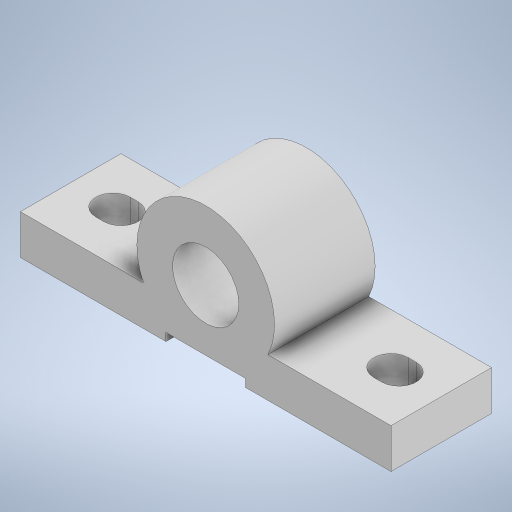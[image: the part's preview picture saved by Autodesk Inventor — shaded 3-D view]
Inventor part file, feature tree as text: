
AUTODESK INVENTOR PART (.ipt)
format: ipt  version: 2023 (Build 270158000, 158)  size: 265,728 bytes
history: native  units: mm
features: extrude x2, sketch x2, other x1
ambient origin geometry x8: Origin, YZ Plane, XZ Plane, XY Plane, X Axis, Y Axis, Z Axis, Center Point
bodies: Body1 (feature_tree)
feature tree (5):
  other  "Твердое тело1"
  extrude  "Выдавливание1"  Depth=25.0mm
  extrude  "Выдавливание2"  Depth=52.0mm
  sketch  "Эскиз1"
  sketch  "Эскиз2"
